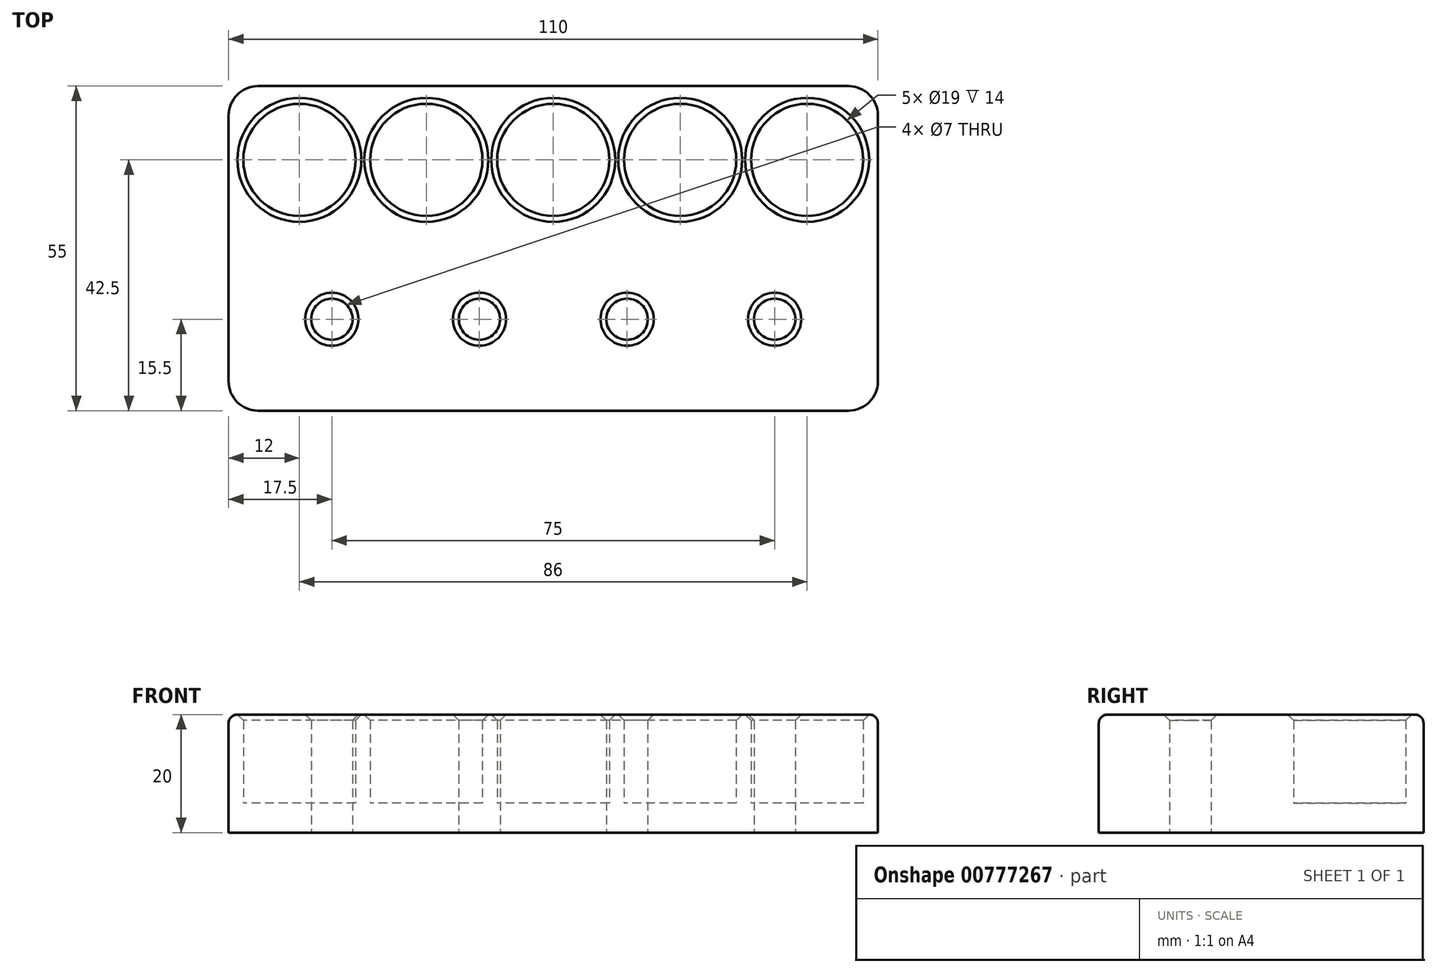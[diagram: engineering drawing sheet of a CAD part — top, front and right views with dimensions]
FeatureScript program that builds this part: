
annotation { "Feature Type Name" : "Feature", "Feature Type Description" : "" }
export const myFeature = defineFeature(function(context is Context, id is Id, definition is map)
    precondition{}
    {
        {
            var Q0;
            Q0=qCreatedBy(makeId("Top.planeOp"),FACE);
            var sketch = newSketch(context, id + "F0", { "sketchPlane" : qUnion([Q0])});
            skLineSegment(sketch, "E0.bottom", {"start": v(-50, 27.5) * mm, "end": v(50, 27.5) * mm});
            skLineSegment(sketch, "E0.top", {"start": v(-50, -27.5) * mm, "end": v(50, -27.5) * mm});
            skLineSegment(sketch, "E0.left", {"start": v(-55, 22.5) * mm, "end": v(-55, -22.5) * mm});
            skLineSegment(sketch, "E0.right", {"start": v(55, 22.5) * mm, "end": v(55, -22.5) * mm});
            skPoint(sketch, "E0.middle", {"position": v(0, 0) * mm});
            skCircle(sketch, "E1", {"center": v(-43, 15) * mm, "radius": 9.5 * mm});
            skCircle(sketch, "E2", {"center": v(-21.5, 15) * mm, "radius": 9.5 * mm});
            skCircle(sketch, "E3", {"center": v(0, 15) * mm, "radius": 9.5 * mm});
            skCircle(sketch, "E4", {"center": v(21.5, 15) * mm, "radius": 9.5 * mm});
            skCircle(sketch, "E5", {"center": v(-37.5, -12) * mm, "radius": 12.5 * mm});
            skCircle(sketch, "E6", {"center": v(-37.5, -12) * mm, "radius": 3.5 * mm});
            skCircle(sketch, "E7", {"center": v(-12.5, -12) * mm, "radius": 12.5 * mm});
            skCircle(sketch, "E8", {"center": v(-12.5, -12) * mm, "radius": 3.5 * mm});
            skCircle(sketch, "E9", {"center": v(12.5, -12) * mm, "radius": 12.5 * mm});
            skCircle(sketch, "E10", {"center": v(12.5, -12) * mm, "radius": 3.5 * mm});
            skCircle(sketch, "E11", {"center": v(37.5, -12) * mm, "radius": 12.5 * mm});
            skCircle(sketch, "E12", {"center": v(37.5, -12) * mm, "radius": 3.5 * mm});
            skCircle(sketch, "E13", {"center": v(43, 15) * mm, "radius": 9.5 * mm});
            skPoint(sketch, "E14.visualSharp", {"position": v(-55, 27.5) * mm});
            skArc(sketch, "E14.filletArc", {"start": v(-50, 27.5) * mm, "mid": v(-53.54, 26.04) * mm, "end": v(-55, 22.5) * mm});
            skPoint(sketch, "E15.visualSharp", {"position": v(55, 27.5) * mm});
            skArc(sketch, "E15.filletArc", {"start": v(55, 22.5) * mm, "mid": v(53.54, 26.04) * mm, "end": v(50, 27.5) * mm});
            skPoint(sketch, "E16.visualSharp", {"position": v(55, -27.5) * mm});
            skArc(sketch, "E16.filletArc", {"start": v(50, -27.5) * mm, "mid": v(53.54, -26.04) * mm, "end": v(55, -22.5) * mm});
            skPoint(sketch, "E17.visualSharp", {"position": v(-55, -27.5) * mm});
            skArc(sketch, "E17.filletArc", {"start": v(-55, -22.5) * mm, "mid": v(-53.54, -26.04) * mm, "end": v(-50, -27.5) * mm});
            skSolve(sketch);
        }
        {
            var Q0;
            Q0=makeQuery(id+"F0.imprint","IMPRINT",FACE,{"disambiguationData":[TD([[makeQuery(id+"F0.imprint","IMPRINT",EDGE,{"derivedFrom":sQuery(id+"F0.wireOp",EDGE,"E0.bottom")}),-1.0]])]});
            var Q1;
            Q1=makeQuery(id+"F0.imprint","IMPRINT",FACE,{"disambiguationData":[TD([[makeQuery(id+"F0.imprint","IMPRINT",EDGE,{"derivedFrom":sQuery(id+"F0.wireOp",EDGE,"E8")}),-1.0]])]});
            var Q2;
            Q2=makeQuery(id+"F0.imprint","IMPRINT",FACE,{"disambiguationData":[TD([[makeQuery(id+"F0.imprint","IMPRINT",EDGE,{"derivedFrom":sQuery(id+"F0.wireOp",EDGE,"E5")}),1.0]])]});
            var Q3;
            Q3=makeQuery(id+"F0.imprint","IMPRINT",FACE,{"disambiguationData":[TD([[makeQuery(id+"F0.imprint","IMPRINT",EDGE,{"derivedFrom":sQuery(id+"F0.wireOp",EDGE,"E10")}),-1.0]])]});
            var Q4;
            Q4=makeQuery(id+"F0.imprint","IMPRINT",FACE,{"disambiguationData":[TD([[makeQuery(id+"F0.imprint","IMPRINT",EDGE,{"derivedFrom":sQuery(id+"F0.wireOp",EDGE,"E11")}),1.0]])]});
            extrude(context, id + "F1", {"entities" : qUnion([Q0, Q1, Q2, Q3, Q4]), "depth" : 20 * mm, "offsetDistance" : 25 * mm});
        }
        {
            var Q0;
            Q0=makeQuery(id+"F0.imprint","IMPRINT",FACE,{"disambiguationData":[TD([[makeQuery(id+"F0.imprint","IMPRINT",EDGE,{"derivedFrom":sQuery(id+"F0.wireOp",EDGE,"E1")}),1.0]])]});
            var Q1;
            Q1=makeQuery(id+"F0.imprint","IMPRINT",FACE,{"disambiguationData":[TD([[makeQuery(id+"F0.imprint","IMPRINT",EDGE,{"derivedFrom":sQuery(id+"F0.wireOp",EDGE,"E2")}),1.0]])]});
            var Q2;
            Q2=makeQuery(id+"F0.imprint","IMPRINT",FACE,{"disambiguationData":[TD([[makeQuery(id+"F0.imprint","IMPRINT",EDGE,{"derivedFrom":sQuery(id+"F0.wireOp",EDGE,"E3")}),1.0]])]});
            var Q3;
            Q3=makeQuery(id+"F0.imprint","IMPRINT",FACE,{"disambiguationData":[TD([[makeQuery(id+"F0.imprint","IMPRINT",EDGE,{"derivedFrom":sQuery(id+"F0.wireOp",EDGE,"E4")}),1.0]])]});
            var Q4;
            Q4=makeQuery(id+"F0.imprint","IMPRINT",FACE,{"disambiguationData":[TD([[makeQuery(id+"F0.imprint","IMPRINT",EDGE,{"derivedFrom":sQuery(id+"F0.wireOp",EDGE,"E13")}),1.0]])]});
            extrude(context, id + "F2", {"entities" : qUnion([Q0, Q1, Q2, Q3, Q4]), "operationType" : NewBodyOperationType.ADD, "depth" : 5 * mm, "offsetDistance" : 25 * mm});
        }
        {
            var Q0;
            Q0=makeQuery(id+"F1.opExtrude","CAP_EDGE",EDGE,{"disambiguationData":[OSD([sQuery(id+"F0.wireOp",EDGE,"E0.top")])],"isStart":false});
            fillet(context, id + "F3", {"entities" : qUnion([Q0]), "radius" : 1.5 * mm, "tangentPropagation" : true, "allowEdgeOverflow" : false});
        }
        {
            var Q0;
            Q0=makeQuery(id+"F1.opExtrude","CAP_EDGE",EDGE,{"disambiguationData":[OSD([sQuery(id+"F0.wireOp",EDGE,"E1")])],"isStart":false});
            var Q1;
            Q1=makeQuery(id+"F1.opExtrude","CAP_EDGE",EDGE,{"disambiguationData":[OSD([sQuery(id+"F0.wireOp",EDGE,"E2")])],"isStart":false});
            var Q2;
            Q2=makeQuery(id+"F1.opExtrude","CAP_EDGE",EDGE,{"disambiguationData":[OSD([sQuery(id+"F0.wireOp",EDGE,"E3")])],"isStart":false});
            var Q3;
            Q3=makeQuery(id+"F1.opExtrude","CAP_EDGE",EDGE,{"disambiguationData":[OSD([sQuery(id+"F0.wireOp",EDGE,"E4")])],"isStart":false});
            var Q4;
            Q4=makeQuery(id+"F1.opExtrude","CAP_EDGE",EDGE,{"disambiguationData":[OSD([sQuery(id+"F0.wireOp",EDGE,"E13")])],"isStart":false});
            chamfer(context, id + "F4", {"entities" : qUnion([Q0, Q1, Q2, Q3, Q4]), "width" : 1 * mm, "tangentPropagation" : true});
        }
        {
            var Q0;
            Q0=makeQuery(id+"F1.opExtrude","CAP_EDGE",EDGE,{"disambiguationData":[OSD([sQuery(id+"F0.wireOp",EDGE,"E6")])],"isStart":false});
            var Q1;
            Q1=makeQuery(id+"F1.opExtrude","CAP_EDGE",EDGE,{"disambiguationData":[OSD([sQuery(id+"F0.wireOp",EDGE,"E8")])],"isStart":false});
            var Q2;
            Q2=makeQuery(id+"F1.opExtrude","CAP_EDGE",EDGE,{"disambiguationData":[OSD([sQuery(id+"F0.wireOp",EDGE,"E10")])],"isStart":false});
            var Q3;
            Q3=makeQuery(id+"F1.opExtrude","CAP_EDGE",EDGE,{"disambiguationData":[OSD([sQuery(id+"F0.wireOp",EDGE,"E12")])],"isStart":false});
            chamfer(context, id + "F5", {"entities" : qUnion([Q0, Q1, Q2, Q3]), "width" : 1 * mm, "tangentPropagation" : true});
        }
    });
